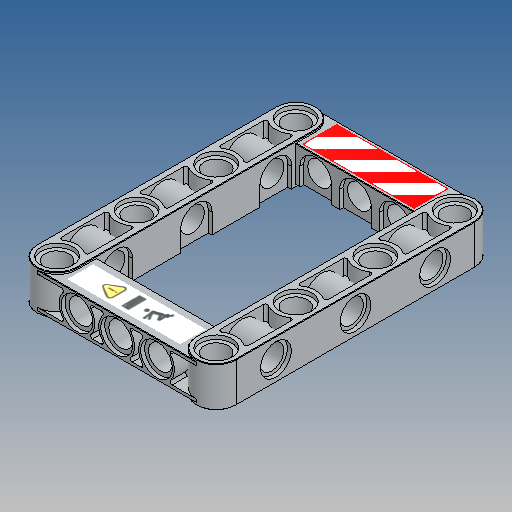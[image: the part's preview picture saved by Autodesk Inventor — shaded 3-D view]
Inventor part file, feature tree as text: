
AUTODESK INVENTOR PART (.ipt)
format: ipt  version: 2025 (Build 290162010, 162A)  size: 1,182,720 bytes
history: native  units: mm
features: extrude x13, sketch x11, other x4, mirror x3, fillet x2, projected_geometry x2, plane x1
ambient origin geometry x8: Origin, YZ Plane, XZ Plane, XY Plane, X Axis, Y Axis, Z Axis, Center Point
bodies: Solid1 (feature_tree)
feature tree (36):
  extrude  "Extrusion1"  Depth=0.8mm TaperAngle=0.0deg
  sketch  "Sketch6"  dims[d43=3.1mm d44=0.0mm d48=48.0mm]
  extrude  "Extrusion7"  Depth=3.1mm
  extrude  "Extrusion8"  Depth=4.8mm
  extrude  "Extrusion19"  Depth=0.4mm
  mirror  "Mirror5"
  sketch  "Sketch7"  dims[d49=6.4mm d50=4.8mm]
  extrude  "Extrusion9"  Depth=10.0mm
  extrude  "Extrusion10"  Depth=10.0mm TaperAngle=0.0deg
  extrude  "Extrusion11"  Depth=10.0mm
  extrude  "Extrusion18"  [1 undecoded]
  fillet  "Fillet2"  Radius=8.0mm
  plane  "Work Plane1"
  extrude  "Extrusion13"  Depth=5.8mm
  sketch  "Sketch12"  dims[d70=4.8mm d71=10.0mm d72=0.0mm]
  extrude  "Extrusion14"  Depth=0.9mm TaperAngle=0.0deg
  extrude  "Extrusion15"  Depth=3.1mm
  extrude  "Extrusion16"  Depth=3.1mm TaperAngle=0.0deg
  extrude  "Extrusion17"  Depth=3.1mm TaperAngle=0.0deg
  fillet  "Fillet3"  Radius=0.8mm
  mirror  "Mirror4"
  mirror  "Mirror3"
  other  "Aufkleber1"
  other  "Aufkleber2"
  projected_geometry  "Projected Loop4"
  sketch  "Skizze - Rechteckige Anordnung1"  dims[d14=8.0mm d15=0.0mm d41=0.8mm d42=0.0mm]
  sketch  "Sketch8"  dims[d51=16.0mm d60=0.4mm d61=0.1mm]
  sketch  "Sketch11"  dims[d62=30.0mm d64=16.0mm d65=10.0mm d67=10.0mm d69=7.2mm]
  projected_geometry  "Projected Loop5"
  sketch  "Sketch13"  dims[d73=10.0mm d74=0.0mm d75=6.2mm]
  sketch  "Sketch14"  dims[d76=0.8mm d77=0.0mm d78=-16.0mm d86=8.0mm]
  sketch  "Sketch15"  dims[d87=3.1mm d88=5.8mm]
  sketch  "Skizze16"  dims[d89=7.2mm d90=0.9mm d91=0.0mm]
  other  "Bild1"
  sketch  "Skizze17"  dims[d92=4.8mm d93=6.4mm d94=0.9mm d95=0.0mm d96=0.9mm d97=0.0mm d98=0.8mm d99=0.0mm d100=6.4mm d101=0.8mm d102=0.0mm d103=0.1mm d104=0.4mm d106=6.4mm d107=0.8mm d108=0.0mm d109=45.0deg d111=1.6mm d112=3.1mm d113=0.0mm d114=16.0mm d116=45.0deg d117=56.0mm d118=8.0mm d125=1.4mm d128=1.4mm d131=0.5mm d133=0.5mm]
  other  "Bild3"
note: 1 required parameter value undecoded (feature->parameter linkage not recoverable at this tier; creation-order binding heuristic only, values carry confidence <= 0.55)
